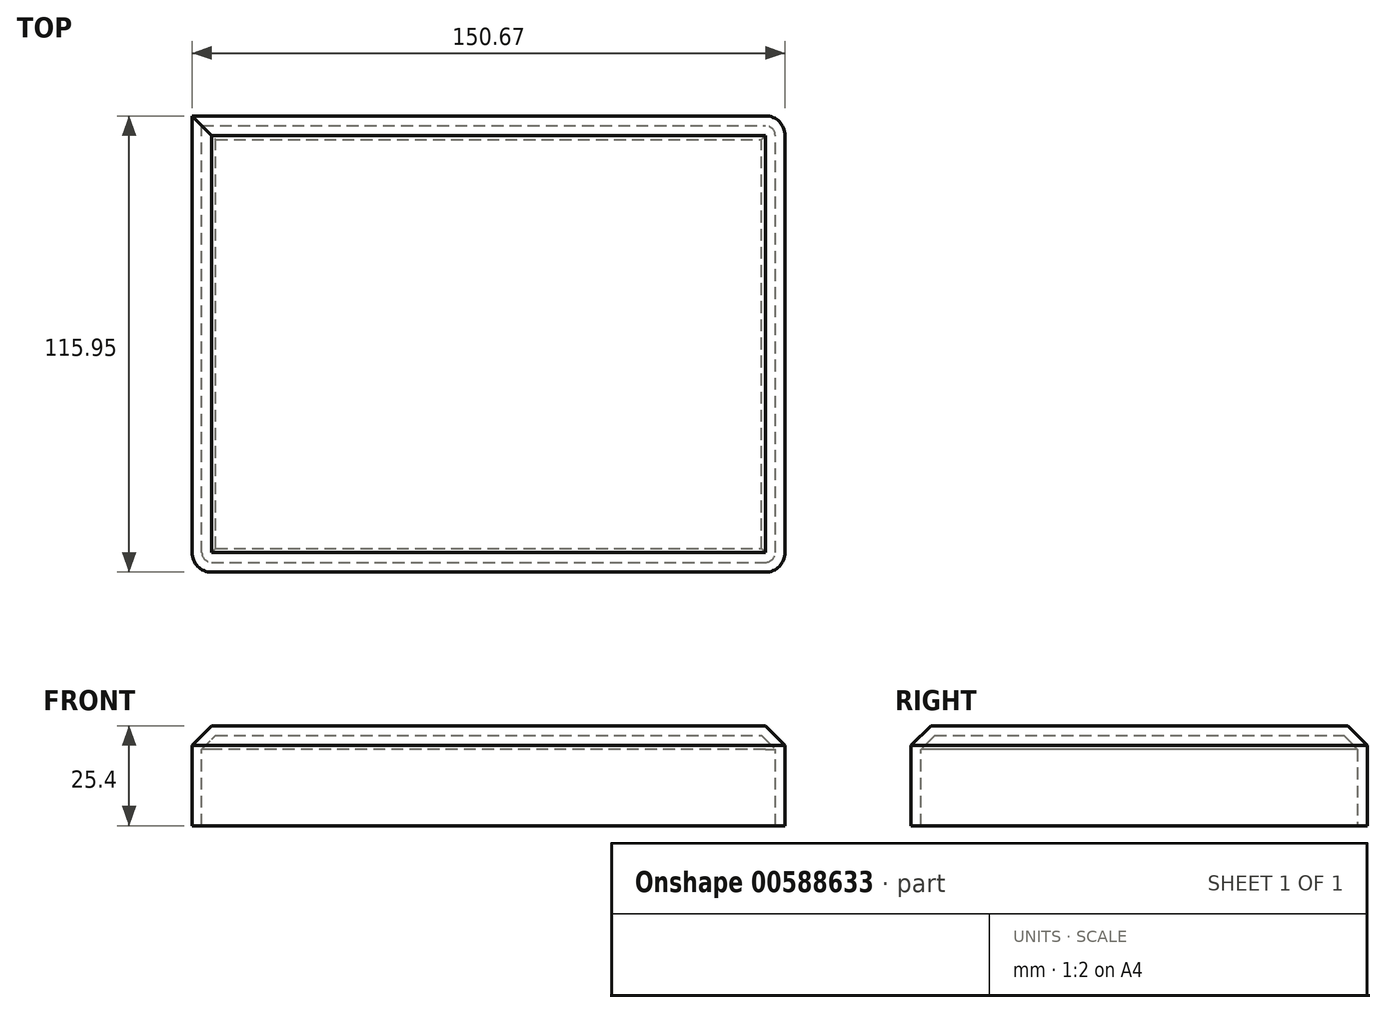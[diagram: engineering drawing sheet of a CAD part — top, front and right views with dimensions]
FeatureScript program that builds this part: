
annotation { "Feature Type Name" : "Feature", "Feature Type Description" : "" }
export const myFeature = defineFeature(function(context is Context, id is Id, definition is map)
    precondition{}
    {
        {
            var Q0;
            Q0=qCreatedBy(makeId("Top.planeOp"),FACE);
            var sketch = newSketch(context, id + "F0", { "sketchPlane" : qUnion([Q0])});
            skLineSegment(sketch, "E0.bottom", {"start": v(-76.08, -39.92) * mm, "end": v(74.6, -39.92) * mm});
            skLineSegment(sketch, "E0.top", {"start": v(-76.08, 76.03) * mm, "end": v(74.6, 76.03) * mm});
            skLineSegment(sketch, "E0.left", {"start": v(-76.08, -39.92) * mm, "end": v(-76.08, 76.03) * mm});
            skLineSegment(sketch, "E0.right", {"start": v(74.6, -39.92) * mm, "end": v(74.6, 76.03) * mm});
            skSolve(sketch);
        }
        {
            var Q0;
            Q0=makeQuery(id+"F0.imprint","IMPRINT",FACE,{"disambiguationData":[TD([[makeQuery(id+"F0.imprint","IMPRINT",EDGE,{"derivedFrom":sQuery(id+"F0.wireOp",EDGE,"E0.bottom")}),1.0]])]});
            extrude(context, id + "F1", {"entities" : qUnion([Q0]), "depth" : 25.4 * mm, "offsetDistance" : 25.4 * mm});
        }
        {
            var Q0;
            Q0=makeQuery(id+"F1.opExtrude","SWEPT_EDGE",EDGE,{"disambiguationData":[OSD([sQuery(id+"F0.wireOp",EDGE,"E0.bottom"),sQuery(id+"F0.wireOp",EDGE,"E0.left")])]});
            var Q1;
            Q1=makeQuery(id+"F1.opExtrude","SWEPT_EDGE",EDGE,{"disambiguationData":[OSD([sQuery(id+"F0.wireOp",EDGE,"E0.bottom"),sQuery(id+"F0.wireOp",EDGE,"E0.right")])]});
            var Q2;
            Q2=makeQuery(id+"F1.opExtrude","SWEPT_EDGE",EDGE,{"disambiguationData":[OSD([sQuery(id+"F0.wireOp",EDGE,"E0.top"),sQuery(id+"F0.wireOp",EDGE,"E0.right")])]});
            fillet(context, id + "F2", {"entities" : qUnion([Q0, Q1, Q2]), "radius" : 5 * mm, "tangentPropagation" : true, "allowEdgeOverflow" : false});
        }
        {
            var Q0;
            Q0=makeQuery(id+"F1.opExtrude","CAP_FACE",FACE,{"disambiguationData":[OSD([sQuery(id+"F0.wireOp",EDGE,"E0.bottom"),sQuery(id+"F0.wireOp",EDGE,"E0.top"),sQuery(id+"F0.wireOp",EDGE,"E0.left"),sQuery(id+"F0.wireOp",EDGE,"E0.right")])],"isStart":false});
            chamfer(context, id + "F3", {"entities" : qUnion([Q0]), "width" : 5 * mm, "tangentPropagation" : true});
        }
        {
            var Q0;
            Q0=makeQuery(id+"F1.opExtrude","CAP_FACE",FACE,{"disambiguationData":[OSD([sQuery(id+"F0.wireOp",EDGE,"E0.bottom"),sQuery(id+"F0.wireOp",EDGE,"E0.top"),sQuery(id+"F0.wireOp",EDGE,"E0.left"),sQuery(id+"F0.wireOp",EDGE,"E0.right")])],"isStart":true});
            shell(context, id + "F4", {"entities" : qUnion([Q0]), "thickness" : 2.5 * mm});
        }
    });
